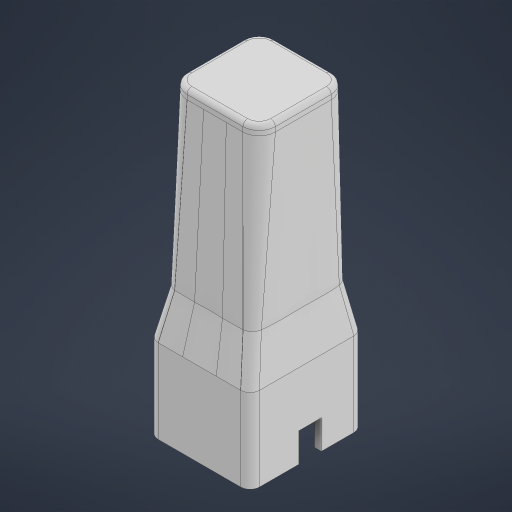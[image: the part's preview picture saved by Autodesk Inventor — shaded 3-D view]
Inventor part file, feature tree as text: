
AUTODESK INVENTOR PART (.ipt)
format: ipt  version: 2024.1 (Build 281209000, 209)  size: 3,538,944 bytes
history: native  units: mm
features: sketch x11, extrude x7, projected_geometry x6, loft x4, boolean_combine x4, other x3, fillet x2, plane x1
ambient origin geometry x8: Origin, YZ Plane, XZ Plane, XY Plane, X Axis, Y Axis, Z Axis, Center Point
bodies: Solid2 (feature_tree), Solid3 (feature_tree), Solid4 (feature_tree), Solid5 (feature_tree), Solid6 (feature_tree), Solid1 (feature_tree)
feature tree (38):
  other  "TubeHolder YN Continuation.ipt"
  extrude  "Extrusion1"  Depth=30.0mm
  fillet  "Fillet1"  Radius=30.0mm
  extrude  "Extrusion2"  Depth=3.0mm
  sketch  "Sketch3"  dims[d8=50.0mm d9=0.0mm d10=1.0mm]
  extrude  "Extrusion3"  Depth=1.0mm
  plane  "Work Plane1"
  sketch  "Sketch6"  dims[d15=3.0mm d16=28.0mm d17=0.0mm]
  sketch  "Sketch5"  dims[d13=1.0mm d14=1.0mm]
  loft  "Loft1"
  loft  "Loft2"
  boolean_combine  "Combine1"
  sketch  "Sketch7"  dims[d18=19.0mm d19=1.0mm]
  loft  "Loft3"
  loft  "Loft4"
  boolean_combine  "Combine2"
  extrude  "Extrusion4"  TaperAngle=0.0deg  [1 undecoded]
  extrude  "Extrusion5"  TaperAngle=0.0deg  [1 undecoded]
  boolean_combine  "Combine3"
  fillet  "Fillet2"  [1 undecoded]
  extrude  "Extrusion6"  TaperAngle=0.0deg  [1 undecoded]
  boolean_combine  "Combine4"
  extrude  "Extrusion7"  Depth=4.0mm
  other  "Solid1::TubeHolder YN Continuation.ipt"
  other  "TaggingFeature1"
  sketch  "Sketch1"  dims[d0=10.0mm d1=30.0mm d2=30.0mm]
  sketch  "Sketch2"  dims[d3=10.0mm d4=20.0mm d5=0.0mm d6=0.0mm d7=3.0mm]
  projected_geometry  "Projected Loop1"
  sketch  "Sketch4"  dims[d11=1.0mm d12=1.0mm]
  projected_geometry  "Projected Loop2"
  sketch  "Sketch8"  dims[d20=4.0mm d21=0.0mm d22=90.0deg]
  projected_geometry  "Projected Loop3"
  sketch  "Sketch9"  dims[d23=0.0mm d24=90.0deg d25=0.0mm d26=90.0deg d27=0.0mm d28=90.0deg]
  sketch  "Sketch10"  dims[d29=1.0mm d32=0.0mm d33=90.0deg]
  sketch  "Sketch11"  dims[d36=0.0mm d37=90.0deg d38=4.0mm d39=0.0mm d40=90.0deg d41=0.0mm d42=90.0deg d43=1.0mm d44=0.0mm d45=3.0mm d46=0.0mm d47=2.0mm d48=0.0mm d49=0.0mm d50=8.0mm d51=0.0mm]
  projected_geometry  "Project Cut Edges1"
  projected_geometry  "Project Cut Edges2"
  projected_geometry  "Project Cut Edges3"
note: 4 required parameter values undecoded (feature->parameter linkage not recoverable at this tier; creation-order binding heuristic only, values carry confidence <= 0.55)
